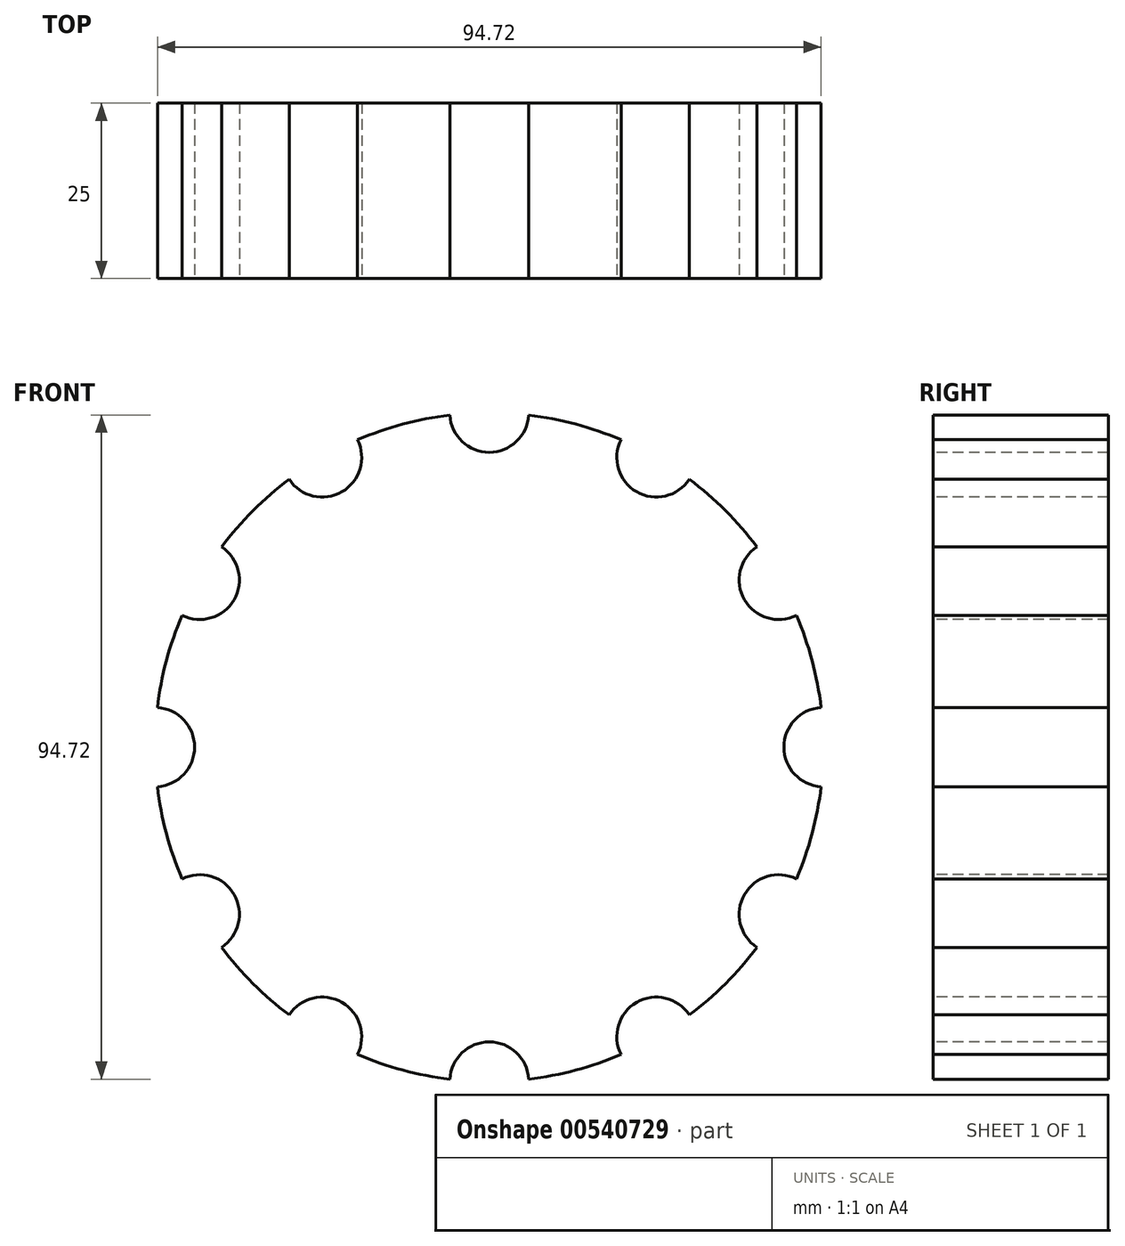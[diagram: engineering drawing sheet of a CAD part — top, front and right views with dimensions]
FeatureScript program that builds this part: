
annotation { "Feature Type Name" : "Feature", "Feature Type Description" : "" }
export const myFeature = defineFeature(function(context is Context, id is Id, definition is map)
    precondition{}
    {
        {
            var Q0;
            Q0=qCreatedBy(makeId("Front.planeOp"),FACE);
            var sketch = newSketch(context, id + "F0", { "sketchPlane" : qUnion([Q0])});
            skCircle(sketch, "E0", {"center": v(0, 0) * mm, "radius": 47.7 * mm});
            skSolve(sketch);
        }
        {
            var Q0;
            Q0=makeQuery(id+"F0.imprint","IMPRINT",FACE,{"disambiguationData":[TD([[makeQuery(id+"F0.imprint","IMPRINT",EDGE,{"derivedFrom":sQuery(id+"F0.wireOp",EDGE,"E0")}),1.0]])]});
            extrude(context, id + "F1", {"entities" : qUnion([Q0]), "depth" : 25 * mm, "offsetDistance" : 25 * mm});
        }
        {
            var Q0;
            Q0=makeQuery(id+"F1.opExtrude","CAP_FACE",FACE,{"disambiguationData":[OSD([sQuery(id+"F0.wireOp",EDGE,"E0")])],"isStart":false});
            var sketch = newSketch(context, id + "F2", { "sketchPlane" : qUnion([Q0])});
            skCircle(sketch, "E1", {"center": v(0, 47.7) * mm, "radius": 5.65 * mm});
            skSolve(sketch);
        }
        {
            var Q0;
            {var subQ0=sQuery(id+"F2.wireOp",EDGE,"E1");var subQ1=makeQuery(id+"F1.opExtrude","CAP_EDGE",EDGE,{"disambiguationData":[OSD([sQuery(id+"F0.wireOp",EDGE,"E0")])],"isStart":false});var subQ2=makeQuery(id+"F2.imprint","INTERSECT",VERTEX,{"disambiguationData":[OD(0.0)],"derivedFrom":[subQ1,subQ0]});Q0=makeQuery(id+"F2.imprint","IMPRINT",FACE,{"disambiguationData":[TD([[makeQuery(id+"F2.imprint","IMPRINT",EDGE,{"disambiguationData":[TD([[subQ2,-1.0]])],"derivedFrom":subQ0}),1.0]])]});}
            extrude(context, id + "F3", {"entities" : qUnion([Q0]), "operationType" : NewBodyOperationType.REMOVE, "oppositeDirection" : true, "depth" : 25 * mm, "offsetDistance" : 25 * mm});
        }
        {
            var Q0;
            Q0=makeQuery(id+"F3.boolean.opBoolean","COPY",FACE,{"derivedFrom":makeQuery(id+"F3.opExtrude","SWEPT_FACE",FACE,{"disambiguationData":[OSD([sQuery(id+"F2.wireOp",EDGE,"E1")])]})});
            var Q1;
            Q1=makeQuery(id+"F1.opExtrude","CAP_EDGE",EDGE,{"disambiguationData":[OSD([sQuery(id+"F0.wireOp",EDGE,"E0")])],"isStart":false});
            circularPattern(context, id + "F4", {"patternType" : PatternType.FACE, "faces" : qUnion([Q0]), "axis" : qUnion([Q1]), "angle" : 360 * degree, "instanceCount" : 12, "equalSpace" : true});
        }
    });
